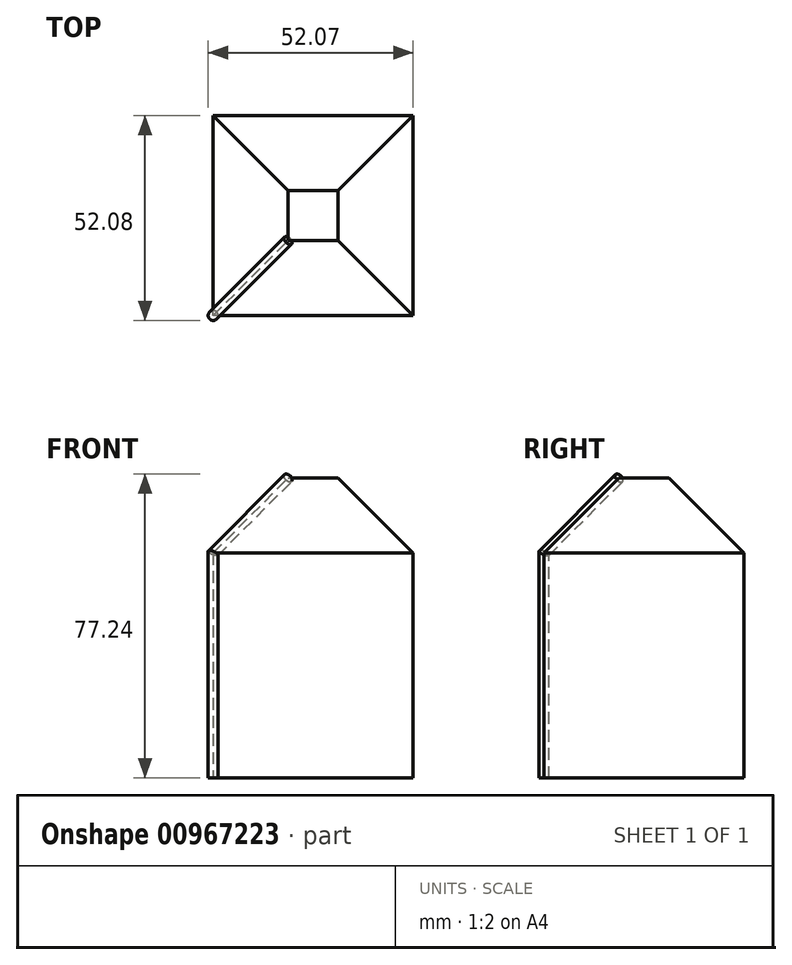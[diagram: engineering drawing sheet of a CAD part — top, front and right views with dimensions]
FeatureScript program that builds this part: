
annotation { "Feature Type Name" : "Feature", "Feature Type Description" : "" }
export const myFeature = defineFeature(function(context is Context, id is Id, definition is map)
    precondition{}
    {
        {
            var Q0;
            Q0=qCreatedBy(makeId("Top.planeOp"),FACE);
            var sketch = newSketch(context, id + "F0", { "sketchPlane" : qUnion([Q0])});
            skLineSegment(sketch, "E0.bottom", {"start": v(25.4, -25.4) * mm, "end": v(-25.4, -25.4) * mm});
            skLineSegment(sketch, "E0.top", {"start": v(25.4, 25.4) * mm, "end": v(-25.4, 25.4) * mm});
            skLineSegment(sketch, "E0.left", {"start": v(25.4, -25.4) * mm, "end": v(25.4, 25.4) * mm});
            skLineSegment(sketch, "E0.right", {"start": v(-25.4, -25.4) * mm, "end": v(-25.4, 25.4) * mm});
            skPoint(sketch, "E0.middle", {"position": v(0, 0) * mm});
            skSolve(sketch);
        }
        {
            var Q0;
            Q0=makeQuery(id+"F0.imprint","IMPRINT",FACE,{"disambiguationData":[TD([[makeQuery(id+"F0.imprint","IMPRINT",EDGE,{"derivedFrom":sQuery(id+"F0.wireOp",EDGE,"E0.bottom")}),-1.0]])]});
            extrude(context, id + "F1", {"entities" : qUnion([Q0]), "depth" : 50.8 * mm, "offsetDistance" : 25.4 * mm});
        }
        {
            var Q0;
            Q0=makeQuery(id+"F1.opExtrude","CAP_FACE",FACE,{"disambiguationData":[OSD([sQuery(id+"F0.wireOp",EDGE,"E0.bottom"),sQuery(id+"F0.wireOp",EDGE,"E0.top"),sQuery(id+"F0.wireOp",EDGE,"E0.left"),sQuery(id+"F0.wireOp",EDGE,"E0.right")])],"isStart":false});
            extrude(context, id + "F2", {"entities" : qUnion([Q0]), "operationType" : NewBodyOperationType.ADD, "depth" : 25.4 * mm, "offsetDistance" : 25.4 * mm});
        }
        {
            var Q0;
            Q0=makeQuery(id+"F2.opExtrude","CAP_EDGE",EDGE,{"disambiguationData":[OSD([sQuery(id+"F0.wireOp",EDGE,"E0.top")])],"isStart":false});
            var Q1;
            Q1=makeQuery(id+"F2.opExtrude","CAP_EDGE",EDGE,{"disambiguationData":[OSD([sQuery(id+"F0.wireOp",EDGE,"E0.left")])],"isStart":false});
            var Q2;
            Q2=makeQuery(id+"F2.opExtrude","CAP_EDGE",EDGE,{"disambiguationData":[OSD([sQuery(id+"F0.wireOp",EDGE,"E0.bottom")])],"isStart":false});
            var Q3;
            Q3=makeQuery(id+"F2.opExtrude","CAP_EDGE",EDGE,{"disambiguationData":[OSD([sQuery(id+"F0.wireOp",EDGE,"E0.right")])],"isStart":false});
            chamfer(context, id + "F3", {"entities" : qUnion([Q0, Q1, Q2, Q3]), "width" : 19.05 * mm, "tangentPropagation" : true});
        }
        {
            var Q0;
            Q0=qCreatedBy(makeId("Top.planeOp"),FACE);
            var sketch = newSketch(context, id + "F4", { "sketchPlane" : qUnion([Q0])});
            skCircle(sketch, "E1", {"center": v(-25.4, -25.4) * mm, "radius": 1.27 * mm});
            skSolve(sketch);
        }
        {
            var Q0;
            Q0 = qSketchRegion(id + "F4", true);
            var Q1;
            {var subQ0=sQuery(id+"F0.wireOp",EDGE,"E0.right");var subQ1=sQuery(id+"F0.wireOp",EDGE,"E0.bottom");Q1=makeQuery(id+"F2.boolean.opBoolean","MERGE",EDGE,{"derivedFrom":[makeQuery(id+"F1.opExtrude","SWEPT_EDGE",EDGE,{"disambiguationData":[OSD([subQ1,subQ0])]}),makeQuery(id+"F2.opExtrude","SWEPT_EDGE",EDGE,{"disambiguationData":[OSD([subQ1,subQ0])]})]});}
            var Q2;
            Q2=makeQuery(id+"F3.opChamfer","BLEND_EDGE",EDGE,{"blendedFrom":[makeQuery(id+"F2.opExtrude","CAP_EDGE",EDGE,{"disambiguationData":[OSD([sQuery(id+"F0.wireOp",EDGE,"E0.bottom")])],"isStart":false}),makeQuery(id+"F2.opExtrude","CAP_EDGE",EDGE,{"disambiguationData":[OSD([sQuery(id+"F0.wireOp",EDGE,"E0.right")])],"isStart":false})],"blendedInto":[]});
            sweep(context, id + "F5", {"profiles" : qUnion([Q0]), "path" : qUnion([Q1, Q2])});
        }
    });
